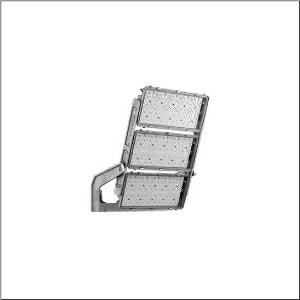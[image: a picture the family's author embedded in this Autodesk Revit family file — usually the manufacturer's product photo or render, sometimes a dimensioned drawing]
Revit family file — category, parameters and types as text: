
# Revit family: floodlight_fl_11_maxi_pro_remote___pl43_5xa779426a01ba_bd65
name_source: partatom
category: Lighting Fixtures
units: mm (PartAtom-declared; Revit-internal decimal feet)

## family parameters
Cut with Voids When Loaded = No
Host = Face
Light Source = No
Part Type = Normal
Room Calculation Point = No
Round Connector Dimension = Use Diameter
Shared = No

## types (1)
- --- (1 x LED, 149370 lm, 1095.8 W, 4000K)
    Apparent Load = 1096 VA
    CIE Flux Codes = 25 74 99 100 100
    Color Rendering = 70
    Color Temperature = 4000K
    Default Elevation = 1800 mm
    Description = Floodlight FL 11  maxi  pro Remote floodlight; light control with lens of PMMA; cover panel of toughened safety glass, transparent; light distribution: PL43, asymmetric direct distribution, LEDcolour temperature: 4000K, rated luminous flux: 149.370lm, colour rendering: CRI > 70, light colour: 740; luminous efficacy: 136lm/W; brightness control: DALI 2 (1 DALI address); with terminal, 8-pole, max. 2.5mm², mains connection: 220..240V/380..400V AC, 50/60Hz, surge voltage resistance: line to ground: 10kV, ECG replaceable separately, no afterglow with DALI off / DMX off command, LED unit replaceable without ESD environment, dustproof LED module, dimming range 10..100%; 1096W floodlight with 2x LED unit of diecast aluminium, coated grey; length: 713mm / width: 651mm / height: 338mm; mounting bracket, of diecast aluminium, uncoated, natural, equipment: Power, protection rating (complete): IP66; insulation class (complete): insulation class I (protective earthing); certification: CE, ENEC, VDE; ball protection: ball impact resistance with accessories, impact resistance: IK07; only for outdoor installations, rated ambient temperature 10°C, permissible operating ambient temperature: -40..+30°C, permissible storage temperature: -40..+85°Cpackaging unit: 1 piece

Light Distribution: PL43
    Height = 320 mm
    Lamp = 1 x LED
    Lamp Light Flux = 149370 lm
    Lamp Power = 1095.8 W
    Lamp count = 1
    Length = 1002 mm
    Luminous efficacy = 136 lm/W
    Manufacturer = Siteco
    ModVariant = No
    Model = 5XA779426A01BA
    Mounting Place = Ceiling
    Mounting Type = Surface mounted
    Number of Poles = 1
    OnlyDefault = Yes
    Power Factor = 1
    Product Name = Floodlight FL 11 maxi pro Remote | PL43
    Product group = floodlight | ceiling mounted
    ProductGroupID = 301
    Protection Class = Protection class I
    Protection Degree = IP 66
    RLX_Detail_Level = 1
    RLX_Emergency_Light_Flux = 0 lm
    RLX_Emergency_Type = 0
    RLX_Emergency_Type_DB = No
    RlxData = <blob elided: 52669 chars, md5=16da50cb>
    Socket = socket
    Standby Power = 0 W
    System Light Flux = 149370 lm
    System Power = 1096 W
    Type Comments = factory setting: luminous flux: 100 % | dim-lin: 254 | 760 mA
    Type Image = l_1349141.jpg
    URL = http://relux.com
    VarID = @adj_096344
    Voltage = 0 V
    Weight = 0.00 kg
    Width = 655 mm

## geometry (parser evidence)
native form markers: Blend x4, Sweep x13
no freeform markers — native parametric forms only
